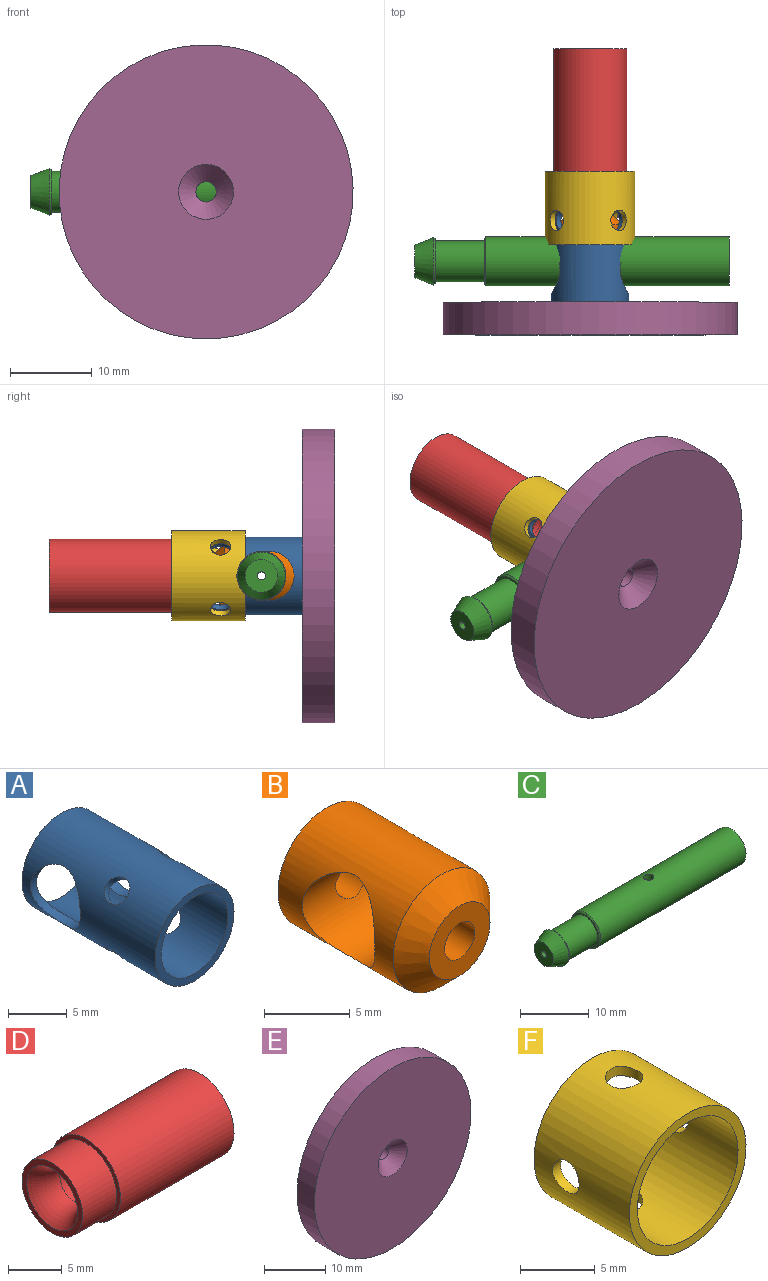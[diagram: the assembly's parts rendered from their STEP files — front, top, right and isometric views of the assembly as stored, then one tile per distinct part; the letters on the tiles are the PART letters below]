
ASSEMBLY  parts=6 mates=6
PART A: 10 faces, bbox 9.5x16x9.5 mm
  f0: cylinder r=4mm len=16mm, axis (0,1,0), area 320.5mm2, adj f2,f3,f4,f5,f6,f7,f8,f9
  f1: cylinder r=4.75mm len=16mm, axis (0,1,0), area 397.8mm2, adj f2,f3,f4,f5,f6,f7,f8,f9
  f2: plane 9.5x9.5mm, normal (0,-1,0), area 20.6mm2, adj f0,f1
  f3: plane 9.5x9.5mm, normal (0,1,0), area 20.6mm2, adj f0,f1
  f4: cylinder r=3mm len=6mm, axis (1,0,0), area 16.5mm2, adj f0,f1
  f5: cylinder r=3mm len=6mm, axis (1,0,0), area 16.5mm2, adj f0,f1
  f6: cylinder r=1.25mm len=2.5mm, axis (0.71,0,0.71), area 6mm2, adj f0,f1
  f7: cylinder r=1.25mm len=2.5mm, axis (0.71,0,0.71), area 6mm2, adj f0,f1
  f8: cylinder r=1.25mm len=2.5mm, axis (-0.71,0,0.71), area 6mm2, adj f0,f1
  f9: cylinder r=1.25mm len=2.5mm, axis (-0.71,0,0.71), area 6mm2, adj f0,f1
PART B: 7 faces, bbox 8x11x8 mm
  f0: cylinder r=3mm len=8mm, axis (1,0,0), area 116.5mm2, adj f1,f5,f6
  f1: cylinder r=4mm len=9.5mm, axis (0,1,0), area 177mm2, adj f0,f3,f4
  f2: plane 5x5mm, normal (0,-1,0), area 14.7mm2, adj f4,f5
  f3: plane 8x8mm, normal (0,1,0), area 45.4mm2, adj f1,f6
  f4: cone r=2.5mm half-angle=45deg, axis (0,1,0), area 43.3mm2, adj f1,f2
  f5: cylinder r=1.25mm len=3.27mm, axis (0,-1,0), area 24.6mm2, adj f0,f2
  f6: cylinder r=1.25mm len=2.5mm, axis (0,-1,0), area 16.8mm2, adj f0,f3
PART C: 15 faces, bbox 38.5x6x6 mm
  f0: cylinder r=1.5mm len=14.4mm, axis (1,0,0), area 133.9mm2, adj f9,f10,f12
  f1: cylinder r=3mm len=29.83mm, axis (1,0,0), area 560.5mm2, adj f4,f12,f13
  f2: cylinder r=0.5mm len=17.9mm, axis (-1,0,0), area 56.2mm2, adj f3,f9
  f3: plane 4x4mm, normal (-1,0,0), area 11.8mm2, adj f2,f8
  f4: plane 6x6mm, normal (1,0,0), area 8.6mm2, adj f1,f11
  f5: plane 5.66x5.66mm, normal (-1,0,0), area 5.5mm2, adj f6,f13
  f6: cylinder r=2.5mm len=6mm, axis (1,0,0), area 94.2mm2, adj f5,f7
  f7: plane 5.5x5.5mm, normal (1,0,0), area 4.1mm2, adj f6,f14
  f8: cone r=2mm half-angle=21.8deg, axis (1,0,0), area 37.7mm2, adj f3,f14
  f9: cone r=0mm half-angle=59deg, axis (1,0,0), area 7.3mm2, adj f0,f2
  f10: cone r=0mm half-angle=59deg, axis (1,0,0), area 14.7mm2, adj f0,f11
  f11: cylinder r=2.5mm len=5mm, axis (1,0,0), area 78.5mm2, adj f4,f10
  f12: cylinder r=0.75mm len=1.7mm, axis (0,0,1), area 7.3mm2, adj f0,f1
  f13: cone r=3mm half-angle=45deg, axis (1,0,0), area 4.4mm2, adj f1,f5
  f14: cone r=2.75mm half-angle=34.1deg, axis (-1,0,0), area 5mm2, adj f7,f8
PART D: 10 faces, bbox 20.5x13x13 mm
  f0: plane 9x9mm, normal (1,0,0), area 13.4mm2, adj f1,f9
  f1: cylinder r=4mm len=8mm, axis (-1,0,0), area 25.1mm2, adj f0,f2
  f2: plane 8x8mm, normal (1,0,0), area 11mm2, adj f1,f3
  f3: cone r=2mm half-angle=7deg, axis (1,0,0), area 219mm2, adj f2,f4
  f4: cylinder r=2mm len=4mm, axis (-1,0,0), area 37.7mm2, adj f3,f5
  f5: torus R=6mm, axis (-1,0,0), area 52.5mm2, adj f4,f6
  f6: plane 8x8mm, normal (-1,0,0), area 14.9mm2, adj f5,f7
  f7: cylinder r=4mm len=8mm, axis (-1,0,0), area 113.1mm2, adj f6,f8
  f8: plane 9x9mm, normal (-1,0,0), area 13.4mm2, adj f7,f9
  f9: cylinder r=4.5mm len=15mm, axis (-1,0,0), area 424.1mm2, adj f0,f8
PART E: 5 faces, bbox 36x4x36 mm
  f0: cylinder r=18mm len=36mm, axis (0,1,0), area 452.4mm2, adj f1,f2
  f1: plane 36x36mm, normal (0,-1,0), area 982.4mm2, adj f0,f4
  f2: plane 36x36mm, normal (0,1,0), area 1013mm2, adj f0,f3
  f3: cylinder r=1.25mm len=2.5mm, axis (0,-1,0), area 14.8mm2, adj f2,f4
  f4: cone r=1.25mm half-angle=45deg, axis (0,-1,0), area 43.2mm2, adj f1,f3
PART F: 8 faces, bbox 11x9x11 mm
  f0: cylinder r=4.75mm len=9.5mm, axis (0,1,0), area 248.8mm2, adj f2,f3,f4,f5,f6,f7
  f1: cylinder r=5.5mm len=11mm, axis (0,1,0), area 291.2mm2, adj f2,f3,f4,f5,f6,f7
  f2: plane 11x11mm, normal (0,-1,0), area 24.2mm2, adj f0,f1
  f3: plane 11x11mm, normal (0,1,0), area 24.2mm2, adj f0,f1
  f4: cylinder r=1.25mm len=2.5mm, axis (1,0,0), area 6mm2, adj f0,f1
  f5: cylinder r=1.25mm len=2.5mm, axis (1,0,0), area 6mm2, adj f0,f1
  f6: cylinder r=1.25mm len=2.5mm, axis (0,0,1), area 6mm2, adj f0,f1
  f7: cylinder r=1.25mm len=2.5mm, axis (0,0,1), area 6mm2, adj f0,f1
PLACE A rot(axis=(1,0,0),180deg) t=(-8.06,-8.68,-12.04)mm
PLACE B rot(axis=(1,0,0),180deg) t=(-8.06,-8.68,-12.04)mm
PLACE C rot(axis=(-1,0,0),90deg) t=(-5.85,-3.68,-12.04)mm
PLACE D rot(axis=(0.58,0.58,0.58),120deg) t=(-8.06,0.22,-12.04)mm
PLACE E t=(-8.06,-8.68,-12.04)mm fixed
PLACE F rot(axis=(0.91,0,0.42),180deg) t=(-8.06,-1.68,-12.04)mm
MATE fastened C.f0 <-> B.f0  axis (1,0,0) through (9,-3.68,-12.04)mm
MATE fastened B.f1 <-> E.f0  axis (0,-1,0) through (-8.06,-8.68,-12.04)mm
MATE fastened D.f1 <-> A.f0  axis (0,-1,0) through (-8.06,7.32,-12.04)mm
MATE revolute F.f0 <-> A.f1  axis (0,-1,0) through (-8.06,7.32,-12.04)mm
MATE fastened A.f0 <-> E.f0  axis (0,-1,0) through (-8.06,-8.68,-12.04)mm
MATE fastened D.f1 <-> A.f1  axis (0,-1,0) through (-8.06,7.32,-12.04)mm
